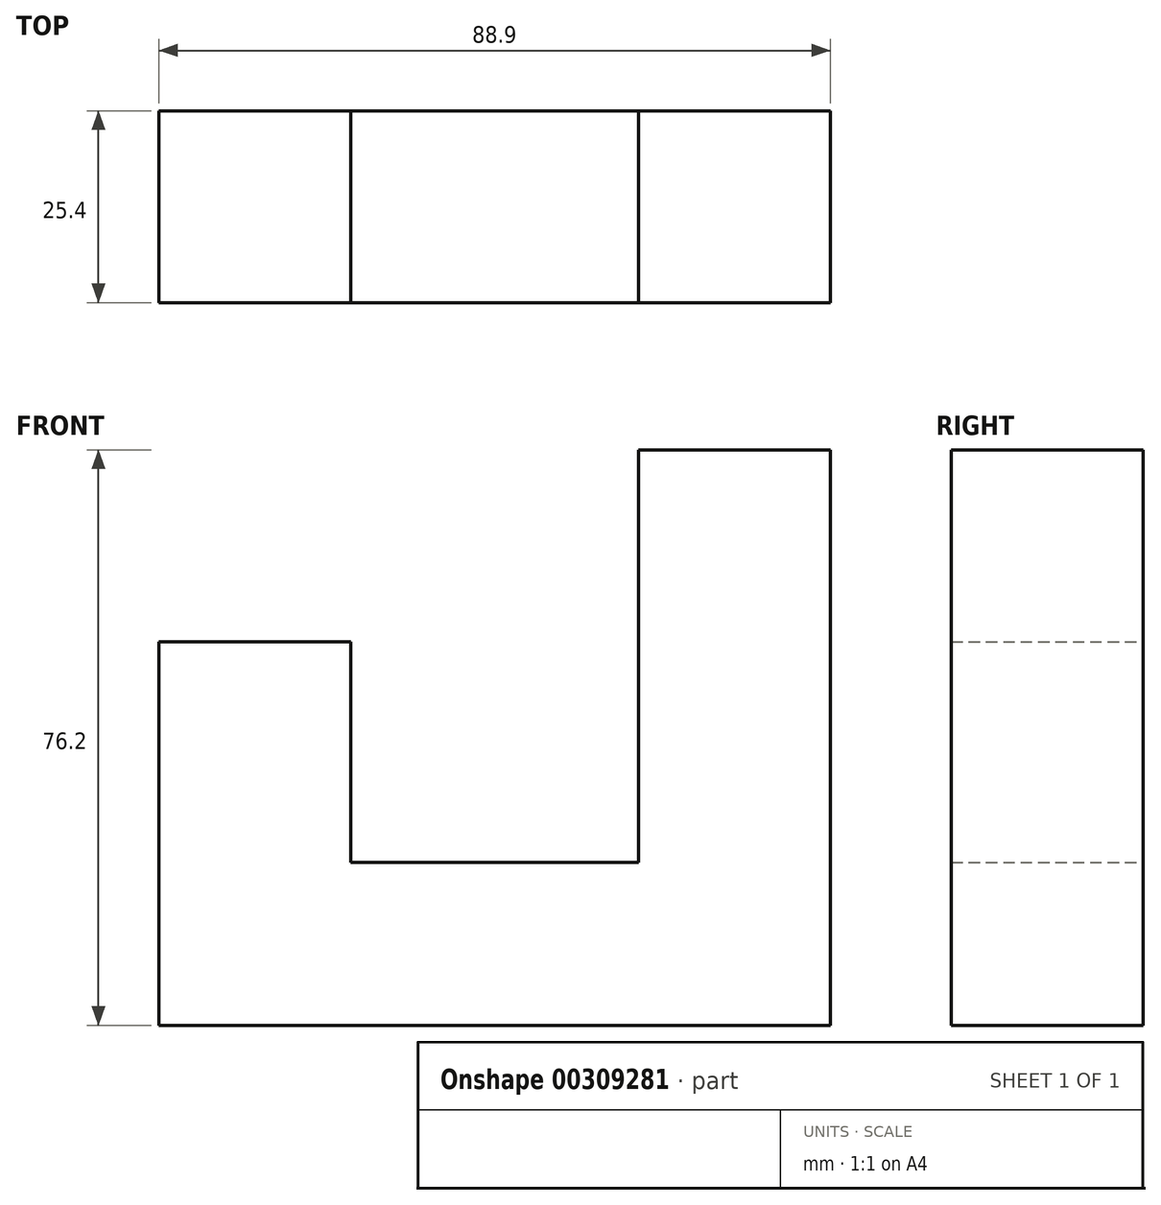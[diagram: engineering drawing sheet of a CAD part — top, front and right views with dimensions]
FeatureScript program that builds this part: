
annotation { "Feature Type Name" : "Feature", "Feature Type Description" : "" }
export const myFeature = defineFeature(function(context is Context, id is Id, definition is map)
    precondition{}
    {
        {
            var Q0;
            Q0=qCreatedBy(makeId("Front.planeOp"),FACE);
            var sketch = newSketch(context, id + "F0", { "sketchPlane" : qUnion([Q0])});
            skLineSegment(sketch, "E0", {"start": v(-41.54, -45.83) * mm, "end": v(47.36, -45.83) * mm});
            skLineSegment(sketch, "E1", {"start": v(47.36, -45.83) * mm, "end": v(47.36, 30.37) * mm});
            skLineSegment(sketch, "E2", {"start": v(47.36, 30.37) * mm, "end": v(21.96, 30.37) * mm});
            skLineSegment(sketch, "E3", {"start": v(21.96, 30.37) * mm, "end": v(21.96, -24.3) * mm});
            skLineSegment(sketch, "E4", {"start": v(21.96, -24.3) * mm, "end": v(-16.14, -24.3) * mm});
            skLineSegment(sketch, "E5", {"start": v(-16.14, -24.3) * mm, "end": v(-16.14, 4.97) * mm});
            skLineSegment(sketch, "E6", {"start": v(-16.14, 4.97) * mm, "end": v(-41.54, 4.97) * mm});
            skLineSegment(sketch, "E7", {"start": v(-41.54, 4.97) * mm, "end": v(-41.54, -45.83) * mm});
            skSolve(sketch);
        }
        {
            var Q0;
            Q0=makeQuery(id+"F0.imprint","IMPRINT",FACE,{"disambiguationData":[TD([[makeQuery(id+"F0.imprint","IMPRINT",EDGE,{"derivedFrom":sQuery(id+"F0.wireOp",EDGE,"E0")}),1.0]])]});
            extrude(context, id + "F1", {"entities" : qUnion([Q0]), "depth" : 25.4 * mm});
        }
    });
